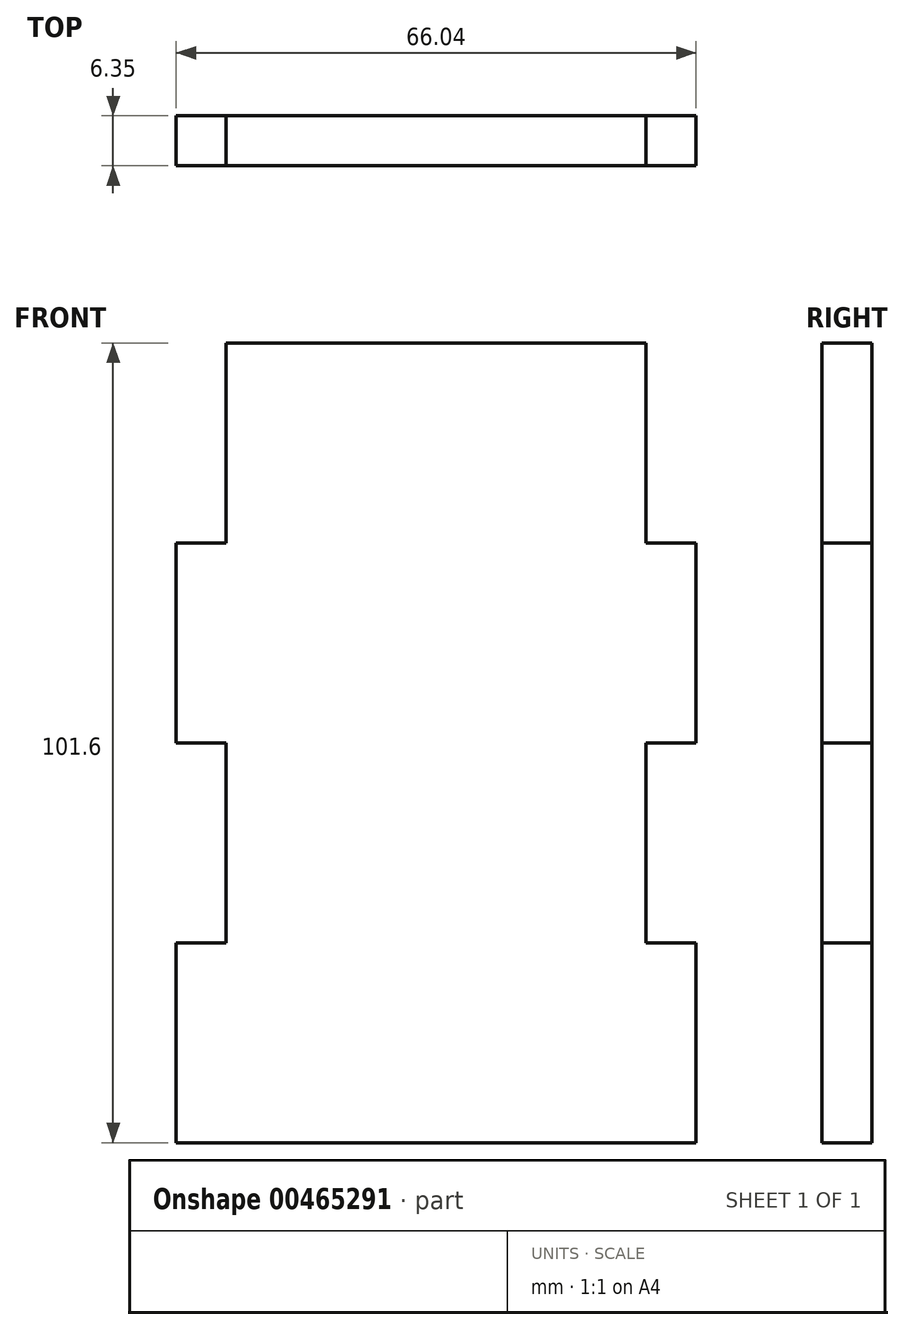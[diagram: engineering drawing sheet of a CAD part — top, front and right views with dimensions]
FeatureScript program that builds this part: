
annotation { "Feature Type Name" : "Feature", "Feature Type Description" : "" }
export const myFeature = defineFeature(function(context is Context, id is Id, definition is map)
    precondition{}
    {
        {
            var Q0;
            Q0=qCreatedBy(makeId("Front.planeOp"),FACE);
            var sketch = newSketch(context, id + "F0", { "sketchPlane" : qUnion([Q0])});
            skLineSegment(sketch, "E0.bottom", {"start": v(26.67, -50.8) * mm, "end": v(-26.67, -50.8) * mm});
            skLineSegment(sketch, "E0.top", {"start": v(26.67, 50.8) * mm, "end": v(-26.67, 50.8) * mm});
            skLineSegment(sketch, "E0.left", {"start": v(26.67, -50.8) * mm, "end": v(26.67, 50.8) * mm});
            skLineSegment(sketch, "E0.right", {"start": v(-26.67, -50.8) * mm, "end": v(-26.67, 50.8) * mm});
            skPoint(sketch, "E0.middle", {"position": v(0, 0) * mm});
            skLineSegment(sketch, "E1.bottom", {"start": v(-26.67, -50.8) * mm, "end": v(-33.02, -50.8) * mm});
            skLineSegment(sketch, "E1.top", {"start": v(-26.67, -25.4) * mm, "end": v(-33.02, -25.4) * mm});
            skLineSegment(sketch, "E1.left", {"start": v(-26.67, -50.8) * mm, "end": v(-26.67, -25.4) * mm});
            skLineSegment(sketch, "E1.right", {"start": v(-33.02, -50.8) * mm, "end": v(-33.02, -25.4) * mm});
            skLineSegment(sketch, "E2.bottom", {"start": v(-26.67, 0) * mm, "end": v(-33.02, 0) * mm});
            skLineSegment(sketch, "E2.top", {"start": v(-26.67, 25.4) * mm, "end": v(-33.02, 25.4) * mm});
            skLineSegment(sketch, "E2.left", {"start": v(-26.67, 0) * mm, "end": v(-26.67, 25.4) * mm});
            skLineSegment(sketch, "E2.right", {"start": v(-33.02, 0) * mm, "end": v(-33.02, 25.4) * mm});
            skLineSegment(sketch, "E3.bottom", {"start": v(26.67, 0) * mm, "end": v(33.02, 0) * mm});
            skLineSegment(sketch, "E3.top", {"start": v(26.67, 25.4) * mm, "end": v(33.02, 25.4) * mm});
            skLineSegment(sketch, "E3.left", {"start": v(26.67, 0) * mm, "end": v(26.67, 25.4) * mm});
            skLineSegment(sketch, "E3.right", {"start": v(33.02, 0) * mm, "end": v(33.02, 25.4) * mm});
            skLineSegment(sketch, "E4.bottom", {"start": v(26.67, -50.8) * mm, "end": v(33.02, -50.8) * mm});
            skLineSegment(sketch, "E4.top", {"start": v(26.67, -25.4) * mm, "end": v(33.02, -25.4) * mm});
            skLineSegment(sketch, "E4.left", {"start": v(26.67, -50.8) * mm, "end": v(26.67, -25.4) * mm});
            skLineSegment(sketch, "E4.right", {"start": v(33.02, -50.8) * mm, "end": v(33.02, -25.4) * mm});
            skSolve(sketch);
        }
        {
            var Q0;
            Q0=makeQuery(id+"F0.imprint","IMPRINT",FACE,{"disambiguationData":[TD([[makeQuery(id+"F0.imprint","IMPRINT",EDGE,{"derivedFrom":sQuery(id+"F0.wireOp",EDGE,"E2.bottom")}),-1.0]])]});
            var Q1;
            Q1=makeQuery(id+"F0.imprint","IMPRINT",FACE,{"disambiguationData":[TD([[makeQuery(id+"F0.imprint","IMPRINT",EDGE,{"derivedFrom":sQuery(id+"F0.wireOp",EDGE,"E0.bottom")}),-1.0]])]});
            var Q2;
            Q2=makeQuery(id+"F0.imprint","IMPRINT",FACE,{"disambiguationData":[TD([[makeQuery(id+"F0.imprint","IMPRINT",EDGE,{"derivedFrom":sQuery(id+"F0.wireOp",EDGE,"E3.bottom")}),1.0]])]});
            var Q3;
            Q3=makeQuery(id+"F0.imprint","IMPRINT",FACE,{"disambiguationData":[TD([[makeQuery(id+"F0.imprint","IMPRINT",EDGE,{"derivedFrom":sQuery(id+"F0.wireOp",EDGE,"E4.bottom")}),1.0]])]});
            var Q4;
            Q4=makeQuery(id+"F0.imprint","IMPRINT",FACE,{"disambiguationData":[TD([[makeQuery(id+"F0.imprint","IMPRINT",EDGE,{"derivedFrom":sQuery(id+"F0.wireOp",EDGE,"E1.bottom")}),-1.0]])]});
            extrude(context, id + "F1", {"entities" : qUnion([Q0, Q1, Q2, Q3, Q4]), "depth" : 6.35 * mm});
        }
    });
